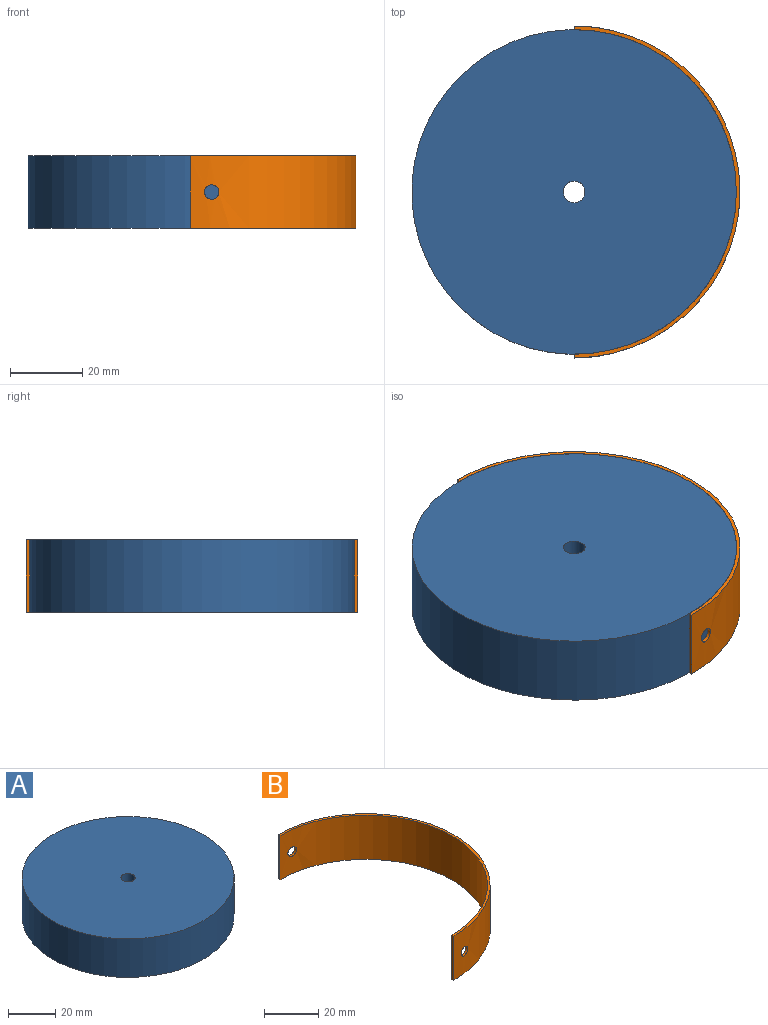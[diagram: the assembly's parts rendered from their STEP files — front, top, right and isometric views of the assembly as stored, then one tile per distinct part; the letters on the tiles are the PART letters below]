
ASSEMBLY  parts=2 mates=1
PART A: 4 faces, bbox 90x90x20 mm
  f0: cylinder r=3mm len=20mm, axis (0,0,-1), area 377mm2, adj f2,f3
  f1: cylinder r=45mm len=90mm, axis (0,0,-1), area 5654.9mm2, adj f2,f3
  f2: plane 90x90mm, normal (0,0,1), area 6333.5mm2, adj f0,f1
  f3: plane 90x90mm, normal (0,0,-1), area 6333.5mm2, adj f0,f1
PART B: 8 faces, bbox 46x92x20 mm
  f0: cylinder r=46mm len=92mm, axis (0,0,-1), area 2864.9mm2, adj f1,f3,f4,f5,f6,f7
  f1: plane 20x1mm, normal (-1,0,0), area 20mm2, adj f0,f2,f4,f5
  f2: cylinder r=45mm len=90mm, axis (0,0,-1), area 2802mm2, adj f1,f3,f4,f5,f6,f7
  f3: plane 20x1mm, normal (-1,0,0), area 20mm2, adj f0,f2,f4,f5
  f4: plane 92x46mm, normal (0,0,1), area 142.9mm2, adj f0,f1,f2,f3
  f5: plane 92x46mm, normal (0,0,-1), area 142.9mm2, adj f0,f1,f2,f3
  f6: cylinder r=2mm len=4mm, axis (0,-1,0), area 12.7mm2, adj f0,f2
  f7: cylinder r=2mm len=4mm, axis (0,-1,0), area 12.7mm2, adj f0,f2
PLACE A t=(16.9,14.66,-22.57)mm
PLACE B t=(16.9,14.66,-22.57)mm
MATE parallel A.f1 <-> B.f2  axis (0,0,-1) through (16.9,14.66,-12.57)mm
